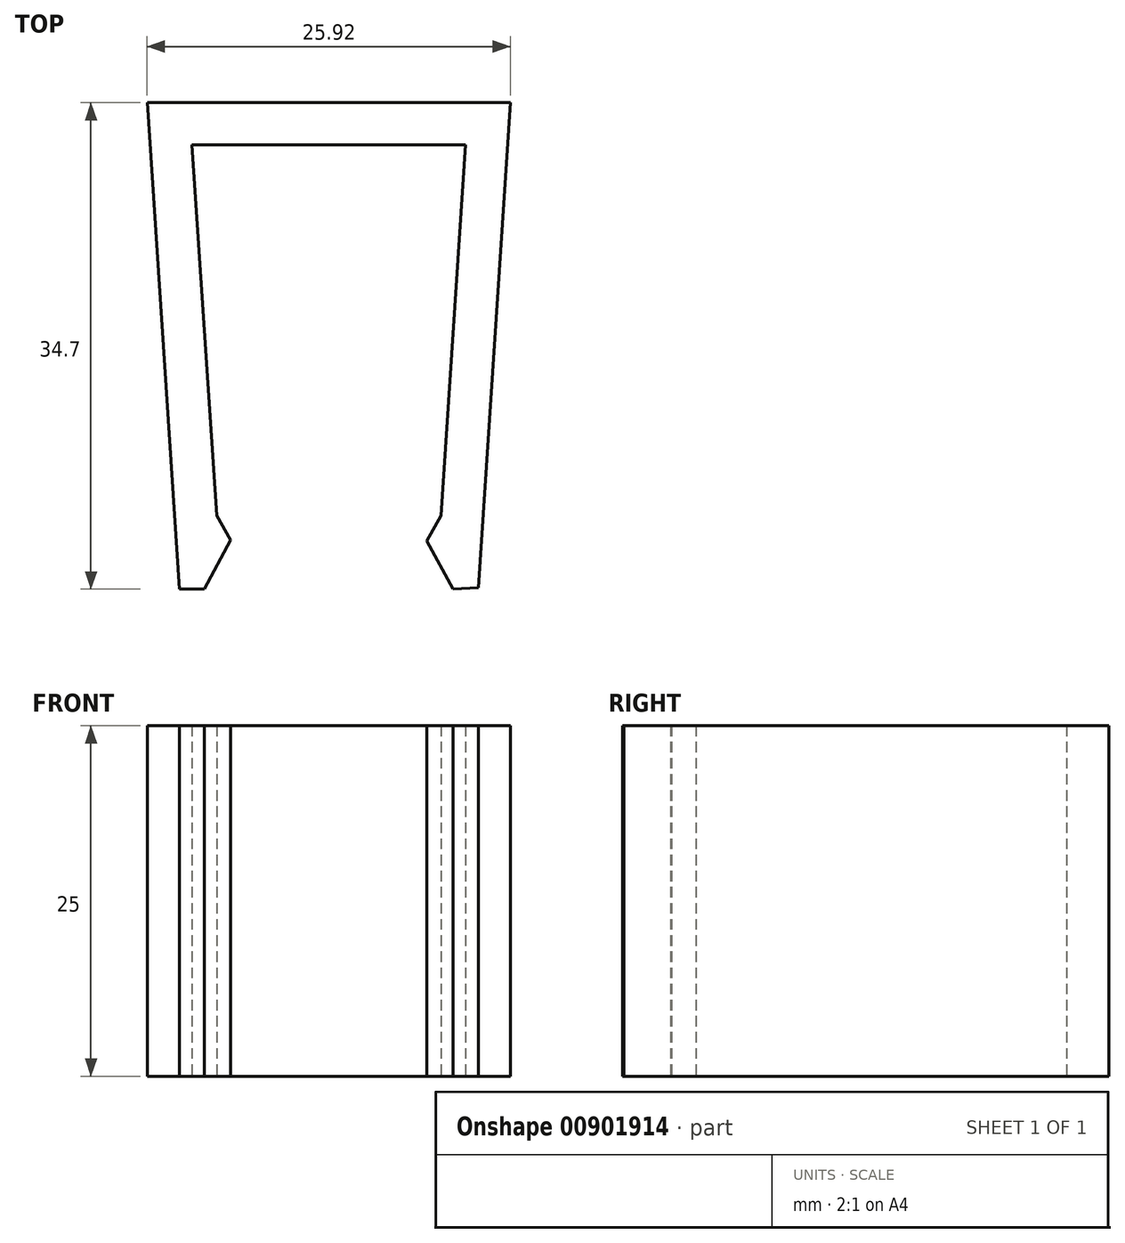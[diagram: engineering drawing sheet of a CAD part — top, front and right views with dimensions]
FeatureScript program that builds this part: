
annotation { "Feature Type Name" : "Feature", "Feature Type Description" : "" }
export const myFeature = defineFeature(function(context is Context, id is Id, definition is map)
    precondition{}
    {
        {
            var Q0;
            Q0=qCreatedBy(makeId("Top.planeOp"),FACE);
            var sketch = newSketch(context, id + "F0", { "sketchPlane" : qUnion([Q0])});
            skLineSegment(sketch, "E0", {"start": v(-9.75, 18.57) * mm, "end": v(9.75, 18.57) * mm});
            skLineSegment(sketch, "E1", {"start": v(9.75, 18.57) * mm, "end": v(8, -7.88) * mm});
            skLineSegment(sketch, "E2", {"start": v(-8, -7.88) * mm, "end": v(-9.75, 18.57) * mm});
            skLineSegment(sketch, "E3", {"start": v(-10.66, -13.13) * mm, "end": v(-12.96, 21.57) * mm});
            skLineSegment(sketch, "E4", {"start": v(-12.96, 21.57) * mm, "end": v(12.96, 21.57) * mm});
            skLineSegment(sketch, "E5", {"start": v(12.96, 21.57) * mm, "end": v(10.67, -13.02) * mm});
            skLineSegment(sketch, "E6", {"start": v(-8, -7.88) * mm, "end": v(-8, -9.63) * mm, "construction": true});
            skLineSegment(sketch, "E7", {"start": v(-8, -9.63) * mm, "end": v(-7, -9.63) * mm, "construction": true});
            skLineSegment(sketch, "E8", {"start": v(-8, -7.88) * mm, "end": v(-7, -9.63) * mm});
            skLineSegment(sketch, "E9", {"start": v(-7, -9.63) * mm, "end": v(-8.87, -13.13) * mm});
            skLineSegment(sketch, "E10", {"start": v(-8.87, -13.13) * mm, "end": v(-10.66, -13.13) * mm});
            skPoint(sketch, "E11.orphan", {"position": v(-10.37, -17.55) * mm});
            skLineSegment(sketch, "E12", {"start": v(8, -7.88) * mm, "end": v(8, -9.7) * mm, "construction": true});
            skLineSegment(sketch, "E13", {"start": v(8, -9.7) * mm, "end": v(7, -9.7) * mm, "construction": true});
            skLineSegment(sketch, "E14", {"start": v(8, -7.88) * mm, "end": v(7, -9.7) * mm});
            skLineSegment(sketch, "E15", {"start": v(7, -9.7) * mm, "end": v(8.88, -13.13) * mm});
            skLineSegment(sketch, "E16", {"start": v(8.88, -13.13) * mm, "end": v(10.67, -13.02) * mm});
            skPoint(sketch, "E17.orphan", {"position": v(10.37, -17.55) * mm});
            skSolve(sketch);
        }
        {
            var Q0;
            Q0=makeQuery(id+"F0.imprint","IMPRINT",FACE,{"disambiguationData":[TD([[makeQuery(id+"F0.imprint","IMPRINT",EDGE,{"derivedFrom":sQuery(id+"F0.wireOp",EDGE,"E0")}),1.0]])]});
            extrude(context, id + "F1", {"entities" : qUnion([Q0]), "depth" : 25 * mm, "offsetDistance" : 25 * mm});
        }
    });
